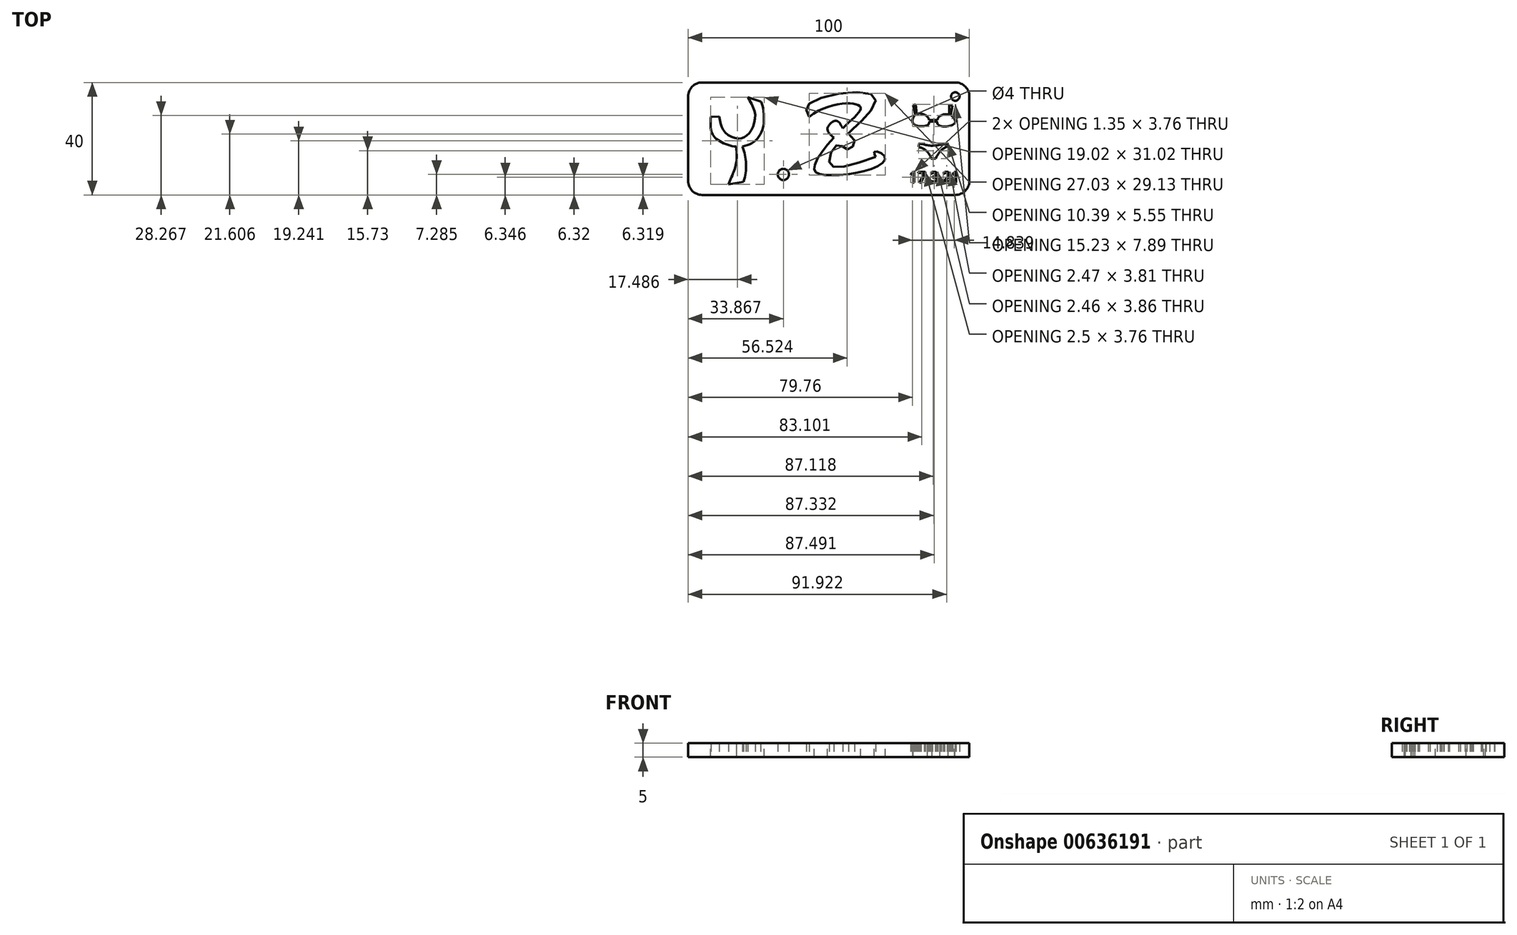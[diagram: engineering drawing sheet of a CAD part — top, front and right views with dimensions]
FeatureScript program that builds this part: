
annotation { "Feature Type Name" : "Feature", "Feature Type Description" : "" }
export const myFeature = defineFeature(function(context is Context, id is Id, definition is map)
    precondition{}
    {
        {
            var Q0;
            Q0=qCreatedBy(makeId("Top.planeOp"),FACE);
            var sketch = newSketch(context, id + "F0", { "sketchPlane" : qUnion([Q0])});
            skLineSegment(sketch, "E0.bottom", {"start": v(5, 0) * mm, "end": v(95, 0) * mm});
            skLineSegment(sketch, "E0.top", {"start": v(5, 40) * mm, "end": v(95, 40) * mm});
            skLineSegment(sketch, "E0.left", {"start": v(0, 5) * mm, "end": v(0, 35) * mm});
            skLineSegment(sketch, "E0.right", {"start": v(100, 5) * mm, "end": v(100, 35) * mm});
            skFitSpline(sketch, "E1", {"points": [v(11.09, 27.94) * mm, v(12.86, 22.61) * mm, v(17.98, 20.01) * mm, v(21.75, 22.02) * mm, v(23.82, 28.53) * mm, v(21.15, 34.75) * mm], "startDerivative": vector(5.02, -30.2) * mm, "endDerivative": vector(-16.99, 26.9) * mm});
            skArc(sketch, "E2", {"start": v(19.74, 4.7) * mm, "mid": v(20.6, 11.01) * mm, "end": v(19.32, 17.26) * mm});
            skCircle(sketch, "E3", {"center": v(33.87, 7.29) * mm, "radius": 2 * mm});
            skFitSpline(sketch, "E4", {"points": [v(43, 27.8) * mm, v(61.15, 31.44) * mm, v(54.95, 23.7) * mm, v(44.82, 9.2) * mm, v(49.38, 7.07) * mm, v(66.51, 9.81) * mm, v(69.85, 13.77) * mm, v(66.22, 15.3) * mm, v(66.63, 13.56) * mm], "startDerivative": vector(114.14, 88.48) * mm, "endDerivative": vector(0.29, -16.44) * mm});
            skCircle(sketch, "E5", {"center": v(95, 35) * mm, "radius": 1.5 * mm});
            skText(sketch, "E6", { "text": "17.3.21", "fontName": "OpenSans-Regular.ttf"});
            skFitSpline(sketch, "E7", {"points": [v(8.13, 27.76) * mm, v(9, 21.07) * mm, v(17.1, 17.2) * mm, v(23.62, 19.13) * mm, v(26.96, 25.96) * mm, v(25.9, 33.21) * mm, v(25.73, 33.21) * mm], "startDerivative": vector(-3.58, -39.12) * mm, "endDerivative": vector(-5.57, -2.82) * mm});
            skLineSegment(sketch, "E8", {"start": v(8.13, 27.76) * mm, "end": v(11.09, 27.94) * mm});
            skLineSegment(sketch, "E9", {"start": v(21.15, 34.75) * mm, "end": v(25.73, 33.21) * mm});
            skFitSpline(sketch, "E10", {"points": [v(17.1, 17.2) * mm, v(17.1, 11.43) * mm, v(14.33, 3.73) * mm], "startDerivative": vector(1.17, -12.29) * mm, "endDerivative": vector(-6.5, -14.57) * mm});
            skLineSegment(sketch, "E11", {"start": v(14.33, 3.73) * mm, "end": v(19.74, 4.7) * mm});
            skFitSpline(sketch, "E12", {"points": [v(43, 27.8) * mm, v(43, 32.45) * mm, v(66.28, 34.97) * mm, v(58.88, 23.72) * mm, v(57.1, 21.5) * mm, v(59.18, 19.28) * mm, v(56.81, 16.17) * mm, v(53.26, 17.8) * mm, v(50.3, 11.13) * mm, v(66.63, 13.56) * mm], "startDerivative": vector(-29.8, 55.17) * mm, "endDerivative": vector(139.76, 51.58) * mm});
            skFitSpline(sketch, "E13", {"points": [v(54.95, 23.7) * mm, v(52.52, 26.38) * mm, v(49.56, 23.7) * mm, v(51.77, 20.4) * mm], "startDerivative": vector(-6.32, 12.54) * mm, "endDerivative": vector(11.57, -9.7) * mm});
            skPoint(sketch, "E14.visualSharp", {"position": v(100, 40) * mm});
            skArc(sketch, "E14.filletArc", {"start": v(100, 35) * mm, "mid": v(98.54, 38.54) * mm, "end": v(95, 40) * mm});
            skPoint(sketch, "E15.visualSharp", {"position": v(100, 0) * mm});
            skArc(sketch, "E15.filletArc", {"start": v(95, 0) * mm, "mid": v(98.54, 1.46) * mm, "end": v(100, 5) * mm});
            skPoint(sketch, "E16.visualSharp", {"position": v(0, 0) * mm});
            skArc(sketch, "E16.filletArc", {"start": v(0, 5) * mm, "mid": v(1.46, 1.46) * mm, "end": v(5, 0) * mm});
            skPoint(sketch, "E17.visualSharp", {"position": v(0, 40) * mm});
            skArc(sketch, "E17.filletArc", {"start": v(5, 40) * mm, "mid": v(1.46, 38.54) * mm, "end": v(0, 35) * mm});
            skFitSpline(sketch, "E18", {"points": [v(88.7, 26.97) * mm, v(89.94, 28.29) * mm, v(93.28, 28.36) * mm, v(94.78, 25.48) * mm, v(89.15, 24.77) * mm, v(88.7, 26.97) * mm]});
            skFitSpline(sketch, "E19", {"points": [v(85.56, 27.1) * mm, v(85.23, 24.93) * mm, v(80.02, 25.45) * mm, v(80.87, 28.57) * mm, v(83.72, 28.66) * mm, v(85.56, 27.1) * mm]});
            skLineSegment(sketch, "E20", {"start": v(79.95, 31.98) * mm, "end": v(80.82, 28.53) * mm});
            skLineSegment(sketch, "E21", {"start": v(79.95, 31.98) * mm, "end": v(80.87, 32.21) * mm});
            skLineSegment(sketch, "E22", {"start": v(80.87, 32.21) * mm, "end": v(81.3, 28.8) * mm});
            skLineSegment(sketch, "E23", {"start": v(85.73, 26.67) * mm, "end": v(88.6, 26.67) * mm});
            skLineSegment(sketch, "E24", {"start": v(85.82, 26.06) * mm, "end": v(88.52, 26.06) * mm});
            skLineSegment(sketch, "E25", {"start": v(92.88, 32) * mm, "end": v(92.88, 28.53) * mm});
            skLineSegment(sketch, "E26", {"start": v(93.99, 31.78) * mm, "end": v(93.32, 28.34) * mm});
            skPoint(sketch, "E27.orphan", {"position": v(93.28, 28.13) * mm});
            skLineSegment(sketch, "E28", {"start": v(92.88, 32) * mm, "end": v(93.99, 31.78) * mm});
            skFitSpline(sketch, "E29", {"points": [v(82.23, 18.41) * mm, v(87.07, 17.53) * mm, v(92.13, 18.5) * mm, v(92.22, 18.63) * mm], "startDerivative": vector(9.44, -3.1) * mm, "endDerivative": vector(0.25, 1.5) * mm});
            skFitSpline(sketch, "E30", {"points": [v(81.92, 17.1) * mm, v(84.83, 15.6) * mm, v(86.41, 12.96) * mm], "startDerivative": vector(6.36, -2.34) * mm, "endDerivative": vector(2.6, -5.95) * mm});
            skFitSpline(sketch, "E31", {"points": [v(92.31, 17.31) * mm, v(89.9, 15.82) * mm, v(88.04, 12.96) * mm], "startDerivative": vector(-5.4, -2.57) * mm, "endDerivative": vector(-3.08, -5.92) * mm});
            skLineSegment(sketch, "E32", {"start": v(82.23, 18.41) * mm, "end": v(81.92, 17.1) * mm});
            skLineSegment(sketch, "E33", {"start": v(86.41, 12.96) * mm, "end": v(88.04, 12.96) * mm});
            skLineSegment(sketch, "E34", {"start": v(92.31, 17.31) * mm, "end": v(92.13, 18.5) * mm});
            const initialGuessF0  = {"E6": [0.0786, 0.00444, 1, 0, 0.00379]};
            skSetInitialGuess(sketch, initialGuessF0);
            skSolve(sketch);
        }
        {
            var Q0;
            Q0 = qSketchRegion(id + "F0", true);
            extrude(context, id + "F1", {"entities" : qUnion([Q0]), "depth" : 5 * mm, "offsetDistance" : 25 * mm});
        }
    });
